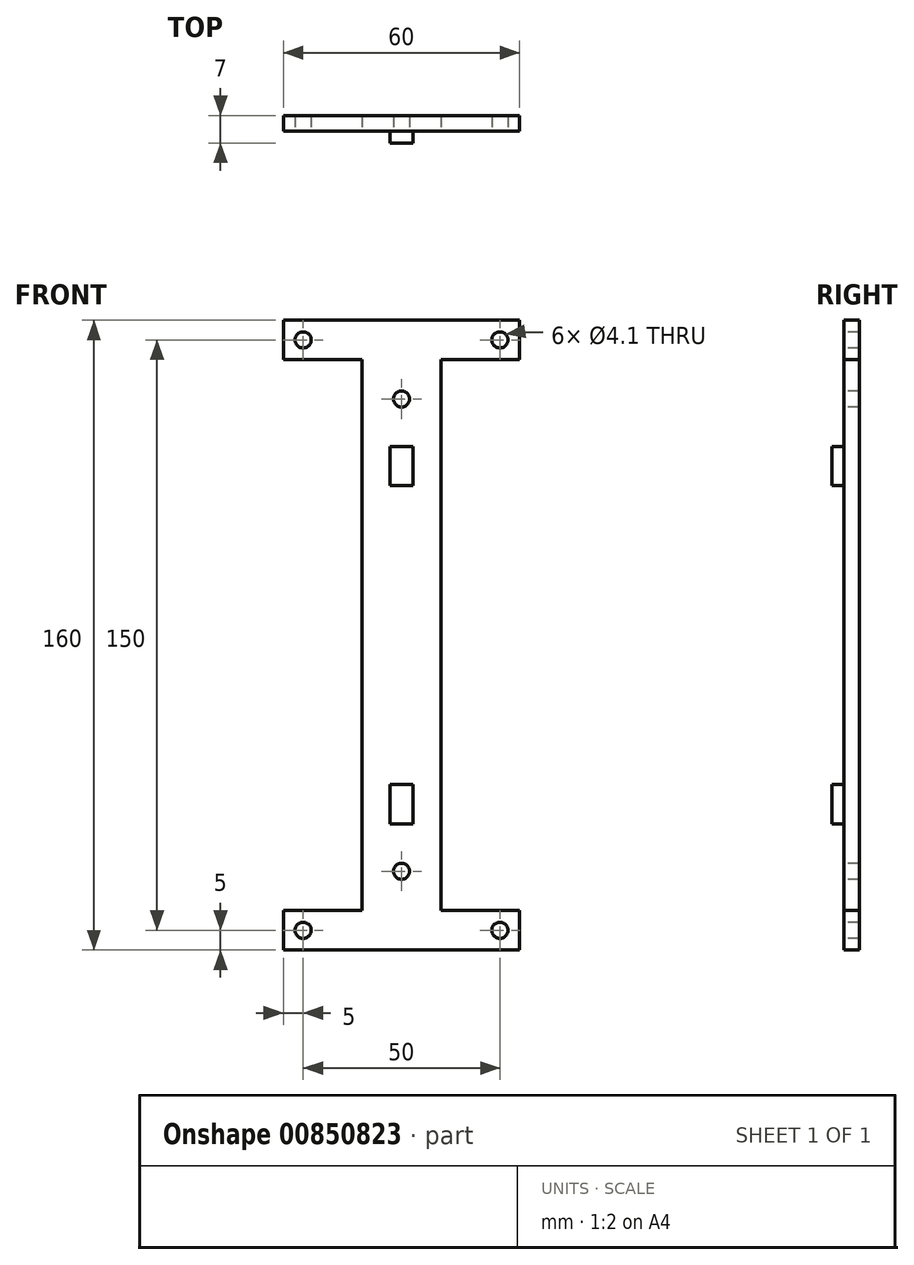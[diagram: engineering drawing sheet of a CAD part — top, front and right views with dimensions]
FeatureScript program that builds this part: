
annotation { "Feature Type Name" : "Feature", "Feature Type Description" : "" }
export const myFeature = defineFeature(function(context is Context, id is Id, definition is map)
    precondition{}
    {
        {
            var Q0;
            Q0=qCreatedBy(makeId("Front.planeOp"),FACE);
            var sketch = newSketch(context, id + "F0", { "sketchPlane" : qUnion([Q0])});
            skLineSegment(sketch, "E0.bottom", {"start": v(-10, 80) * mm, "end": v(10, 80) * mm});
            skLineSegment(sketch, "E0.top", {"start": v(-10, -80) * mm, "end": v(10, -80) * mm});
            skLineSegment(sketch, "E0.left", {"start": v(-10, 80) * mm, "end": v(-10, -80) * mm});
            skLineSegment(sketch, "E0.right", {"start": v(10, 80) * mm, "end": v(10, -80) * mm});
            skPoint(sketch, "E1.firstSnap0", {"position": v(0, -80) * mm});
            skLineSegment(sketch, "E1.bottom", {"start": v(-30, -80) * mm, "end": v(30, -80) * mm});
            skLineSegment(sketch, "E1.top", {"start": v(-30, -70) * mm, "end": v(30, -70) * mm});
            skLineSegment(sketch, "E1.left", {"start": v(-30, -80) * mm, "end": v(-30, -70) * mm});
            skLineSegment(sketch, "E1.right", {"start": v(30, -80) * mm, "end": v(30, -70) * mm});
            skLineSegment(sketch, "E2.bottom", {"start": v(-30, 80) * mm, "end": v(30, 80) * mm});
            skLineSegment(sketch, "E2.top", {"start": v(-30, 70) * mm, "end": v(30, 70) * mm});
            skLineSegment(sketch, "E2.left", {"start": v(-30, 80) * mm, "end": v(-30, 70) * mm});
            skLineSegment(sketch, "E2.right", {"start": v(30, 80) * mm, "end": v(30, 70) * mm});
            skPoint(sketch, "E3", {"position": v(0, 80) * mm});
            skLineSegment(sketch, "E4", {"start": v(-10, 0) * mm, "end": v(10, 0) * mm, "construction": true});
            skLineSegment(sketch, "E5", {"start": v(0, 80) * mm, "end": v(0, -80) * mm, "construction": true});
            skPoint(sketch, "E6", {"position": v(0, 0) * mm});
            skCircle(sketch, "E7", {"center": v(-25, 75) * mm, "radius": 2.05 * mm});
            skCircle(sketch, "E8", {"center": v(25, 75) * mm, "radius": 2.05 * mm});
            skLineSegment(sketch, "E9", {"start": v(-25, 75) * mm, "end": v(25, 75) * mm, "construction": true});
            skCircle(sketch, "E10", {"center": v(-25, -75) * mm, "radius": 2.05 * mm});
            skCircle(sketch, "E11", {"center": v(25, -75) * mm, "radius": 2.05 * mm});
            skLineSegment(sketch, "E12", {"start": v(-25, -75) * mm, "end": v(25, -75) * mm, "construction": true});
            skCircle(sketch, "E13", {"center": v(0, 60) * mm, "radius": 2.05 * mm});
            skCircle(sketch, "E14", {"center": v(0, -60) * mm, "radius": 2.05 * mm});
            skLineSegment(sketch, "E15.bottom", {"start": v(-2.9, 47.95) * mm, "end": v(2.9, 47.95) * mm});
            skLineSegment(sketch, "E15.top", {"start": v(-2.9, 37.95) * mm, "end": v(2.9, 37.95) * mm});
            skLineSegment(sketch, "E15.left", {"start": v(-2.9, 47.95) * mm, "end": v(-2.9, 37.95) * mm});
            skLineSegment(sketch, "E15.right", {"start": v(2.9, 47.95) * mm, "end": v(2.9, 37.95) * mm});
            skPoint(sketch, "E16", {"position": v(0, 47.95) * mm});
            skLineSegment(sketch, "E17.bottom", {"start": v(-2.9, -37.95) * mm, "end": v(2.9, -37.95) * mm});
            skLineSegment(sketch, "E17.top", {"start": v(-2.9, -47.95) * mm, "end": v(2.9, -47.95) * mm});
            skLineSegment(sketch, "E17.left", {"start": v(-2.9, -37.95) * mm, "end": v(-2.9, -47.95) * mm});
            skLineSegment(sketch, "E17.right", {"start": v(2.9, -37.95) * mm, "end": v(2.9, -47.95) * mm});
            skPoint(sketch, "E18", {"position": v(0, -47.95) * mm});
            skSolve(sketch);
        }
        {
            var Q0;
            {var subQ0=sQuery(id+"F0.wireOp",EDGE,"E2.left");Q0=makeQuery(id+"F0.imprint","IMPRINT",FACE,{"disambiguationData":[TD([[makeQuery(id+"F0.imprint","IMPRINT",EDGE,{"derivedFrom":subQ0}),1.0]])]});}
            var Q1;
            {var subQ0=sQuery(id+"F0.wireOp",EDGE,"E2.right");Q1=makeQuery(id+"F0.imprint","IMPRINT",FACE,{"disambiguationData":[TD([[makeQuery(id+"F0.imprint","IMPRINT",EDGE,{"derivedFrom":subQ0}),-1.0]])]});}
            var Q2;
            {var subQ0=sQuery(id+"F0.wireOp",EDGE,"E2.bottom");var subQ1=sQuery(id+"F0.wireOp",EDGE,"E0.left");var subQ2=makeQuery(id+"F0.imprint","INTERSECT",VERTEX,{"derivedFrom":[subQ1,subQ0]});Q2=makeQuery(id+"F0.imprint","IMPRINT",FACE,{"disambiguationData":[TD([[makeQuery(id+"F0.imprint","IMPRINT",EDGE,{"disambiguationData":[TD([[subQ2,-1.0]])],"derivedFrom":subQ1}),1.0]])]});}
            var Q3;
            Q3=makeQuery(id+"F0.imprint","IMPRINT",FACE,{"disambiguationData":[TD([[makeQuery(id+"F0.imprint","IMPRINT",EDGE,{"derivedFrom":sQuery(id+"F0.wireOp",EDGE,"E13")}),-1.0]])]});
            var Q4;
            {var subQ0=sQuery(id+"F0.wireOp",EDGE,"E1.left");Q4=makeQuery(id+"F0.imprint","IMPRINT",FACE,{"disambiguationData":[TD([[makeQuery(id+"F0.imprint","IMPRINT",EDGE,{"derivedFrom":subQ0}),-1.0]])]});}
            var Q5;
            {var subQ0=sQuery(id+"F0.wireOp",EDGE,"E1.bottom");var subQ1=sQuery(id+"F0.wireOp",EDGE,"E0.left");var subQ2=makeQuery(id+"F0.imprint","INTERSECT",VERTEX,{"derivedFrom":[subQ1,subQ0]});Q5=makeQuery(id+"F0.imprint","IMPRINT",FACE,{"disambiguationData":[TD([[makeQuery(id+"F0.imprint","IMPRINT",EDGE,{"disambiguationData":[TD([[subQ2,1.0]])],"derivedFrom":subQ1}),1.0]])]});}
            var Q6;
            {var subQ0=sQuery(id+"F0.wireOp",EDGE,"E1.right");Q6=makeQuery(id+"F0.imprint","IMPRINT",FACE,{"disambiguationData":[TD([[makeQuery(id+"F0.imprint","IMPRINT",EDGE,{"derivedFrom":subQ0}),1.0]])]});}
            var Q7;
            Q7=makeQuery(id+"F0.imprint","IMPRINT",FACE,{"disambiguationData":[TD([[makeQuery(id+"F0.imprint","IMPRINT",EDGE,{"derivedFrom":sQuery(id+"F0.wireOp",EDGE,"E15.bottom")}),-1.0]])]});
            var Q8;
            Q8=makeQuery(id+"F0.imprint","IMPRINT",FACE,{"disambiguationData":[TD([[makeQuery(id+"F0.imprint","IMPRINT",EDGE,{"derivedFrom":sQuery(id+"F0.wireOp",EDGE,"E17.bottom")}),-1.0]])]});
            extrude(context, id + "F1", {"entities" : qUnion([Q0, Q1, Q2, Q3, Q4, Q5, Q6, Q7, Q8]), "oppositeDirection" : true, "depth" : 4 * mm, "offsetDistance" : 25 * mm});
        }
        {
            var Q0;
            Q0=makeQuery(id+"F0.imprint","IMPRINT",FACE,{"disambiguationData":[TD([[makeQuery(id+"F0.imprint","IMPRINT",EDGE,{"derivedFrom":sQuery(id+"F0.wireOp",EDGE,"E15.bottom")}),-1.0]])]});
            var Q1;
            Q1=makeQuery(id+"F0.imprint","IMPRINT",FACE,{"disambiguationData":[TD([[makeQuery(id+"F0.imprint","IMPRINT",EDGE,{"derivedFrom":sQuery(id+"F0.wireOp",EDGE,"E17.bottom")}),-1.0]])]});
            extrude(context, id + "F2", {"entities" : qUnion([Q0, Q1]), "operationType" : NewBodyOperationType.ADD, "depth" : 3 * mm, "offsetDistance" : 25 * mm});
        }
    });
